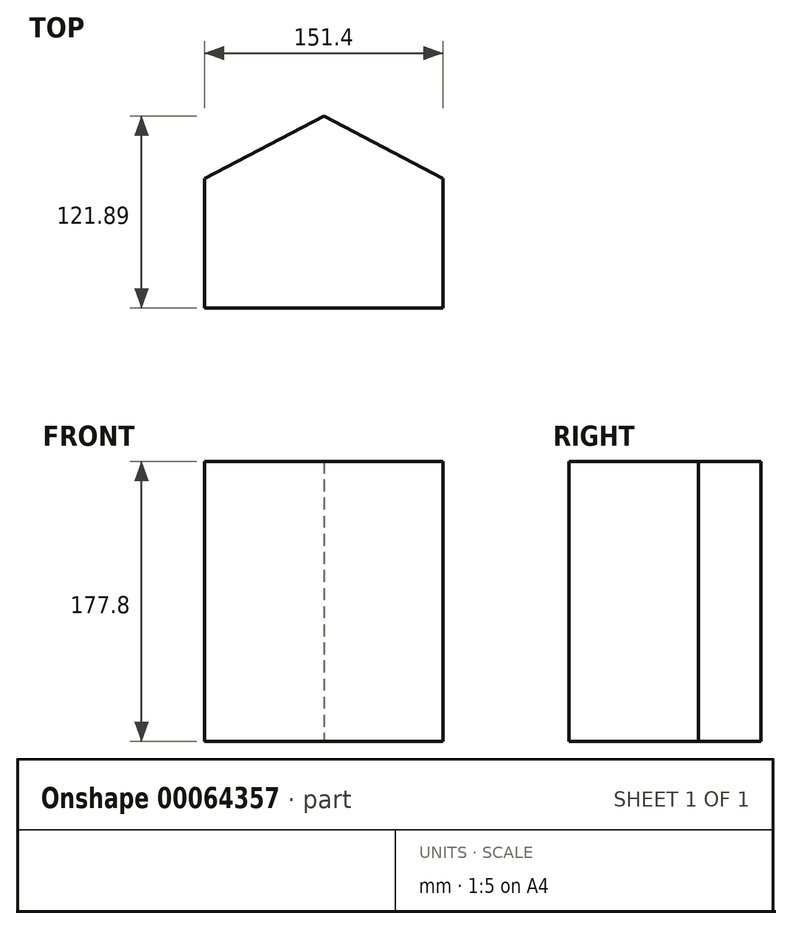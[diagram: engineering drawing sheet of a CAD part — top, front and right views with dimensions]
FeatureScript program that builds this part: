
annotation { "Feature Type Name" : "Feature", "Feature Type Description" : "" }
export const myFeature = defineFeature(function(context is Context, id is Id, definition is map)
    precondition{}
    {
        {
            var Q0;
            Q0=qCreatedBy(makeId("Top.planeOp"),FACE);
            var sketch = newSketch(context, id + "F0", { "sketchPlane" : qUnion([Q0])});
            skLineSegment(sketch, "E0.rect.bottom", {"start": v(-75.7, 35) * mm, "end": v(75.7, 35) * mm});
            skLineSegment(sketch, "E0.rect.top", {"start": v(-75.7, -47.21) * mm, "end": v(75.7, -47.21) * mm});
            skLineSegment(sketch, "E0.rect.left", {"start": v(-75.7, 35) * mm, "end": v(-75.7, -47.21) * mm});
            skLineSegment(sketch, "E0.rect.right", {"start": v(75.7, 35) * mm, "end": v(75.7, -47.21) * mm});
            skPoint(sketch, "E0.rect.middle", {"position": v(0, -6.1) * mm});
            skLineSegment(sketch, "E1", {"start": v(0, 74.68) * mm, "end": v(75.7, 35) * mm});
            skLineSegment(sketch, "E2", {"start": v(0, 74.68) * mm, "end": v(-75.7, 35) * mm});
            skSolve(sketch);
        }
        {
            var Q0;
            Q0 = qSketchRegion(id + "F0", true);
            extrude(context, id + "F1", {"entities" : qUnion([Q0]), "depth" : 177.8 * mm});
        }
    });
